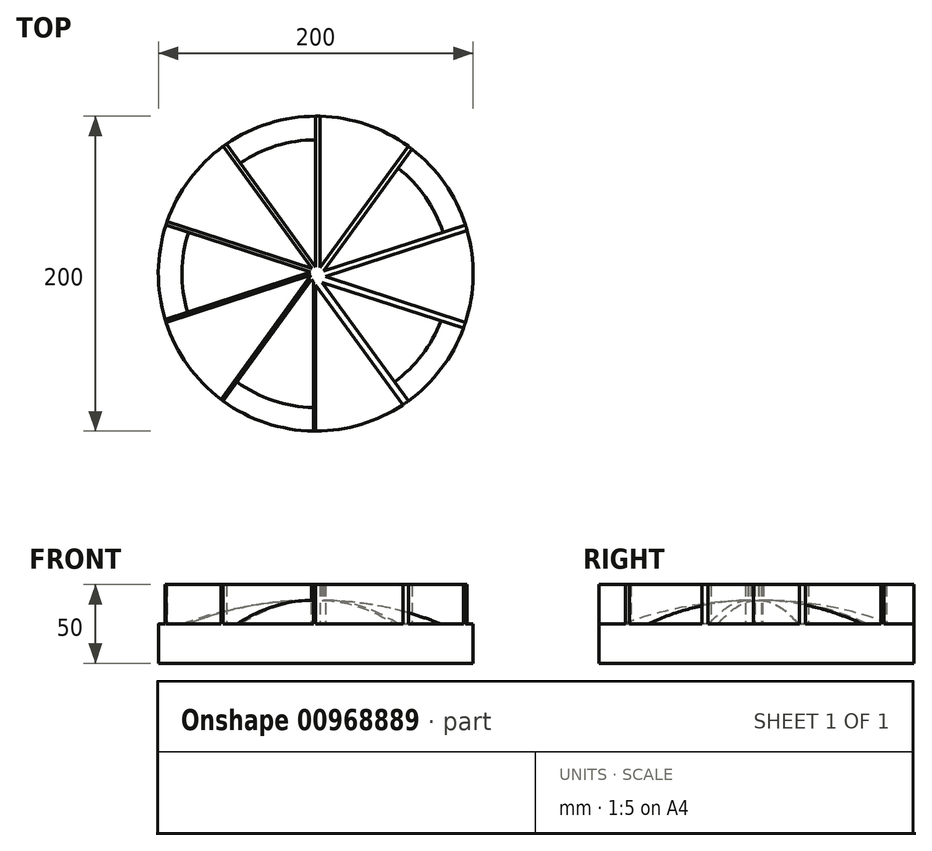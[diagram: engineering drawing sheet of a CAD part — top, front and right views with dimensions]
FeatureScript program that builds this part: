
annotation { "Feature Type Name" : "Feature", "Feature Type Description" : "" }
export const myFeature = defineFeature(function(context is Context, id is Id, definition is map)
    precondition{}
    {
        {
            var Q0;
            Q0=qCreatedBy(makeId("Top.planeOp"),FACE);
            var sketch = newSketch(context, id + "F0", { "sketchPlane" : qUnion([Q0])});
            skCircle(sketch, "E0", {"center": v(0, 0) * mm, "radius": 100 * mm});
            skSolve(sketch);
        }
        {
            var Q0;
            Q0 = qSketchRegion(id + "F0", true);
            extrude(context, id + "F1", {"entities" : qUnion([Q0]), "depth" : 25 * mm, "offsetDistance" : 25 * mm});
        }
        {
            var Q0;
            Q0=makeQuery(id+"F1.opExtrude","CAP_FACE",FACE,{"disambiguationData":[OSD([sQuery(id+"F0.wireOp",EDGE,"E0")])],"isStart":false});
            var sketch = newSketch(context, id + "F2", { "sketchPlane" : qUnion([Q0])});
            skLineSegment(sketch, "E1", {"start": v(0, 0) * mm, "end": v(0, -100) * mm});
            skLineSegment(sketch, "E2.1.0", {"start": v(0, 0) * mm, "end": v(58.78, -80.9) * mm});
            skLineSegment(sketch, "E2.2.0", {"start": v(0, 0) * mm, "end": v(95.1, -30.9) * mm});
            skLineSegment(sketch, "E2.3.0", {"start": v(0, 0) * mm, "end": v(95.1, 30.9) * mm});
            skLineSegment(sketch, "E2.4.0", {"start": v(0, 0) * mm, "end": v(58.78, 80.9) * mm});
            skLineSegment(sketch, "E2.5.0", {"start": v(0, 0) * mm, "end": v(0, 100) * mm});
            skLineSegment(sketch, "E2.6.0", {"start": v(0, 0) * mm, "end": v(-58.78, 80.9) * mm});
            skLineSegment(sketch, "E2.7.0", {"start": v(0, 0) * mm, "end": v(-95.1, 30.9) * mm});
            skLineSegment(sketch, "E2.8.0", {"start": v(0, 0) * mm, "end": v(-95.1, -30.9) * mm});
            skLineSegment(sketch, "E2.9.0", {"start": v(0, 0) * mm, "end": v(-58.78, -80.9) * mm});
            skPoint(sketch, "E2.center", {"position": v(0, 0) * mm});
            skCircle(sketch, "E3", {"center": v(0, 0) * mm, "radius": 2.5 * mm});
            skLineSegment(sketch, "E4.0", {"start": v(-1.5, 0) * mm, "end": v(-1.5, -100) * mm});
            skLineSegment(sketch, "E5.0", {"start": v(-1.42, 1.03) * mm, "end": v(-60.2, -79.87) * mm});
            skLineSegment(sketch, "E6.0", {"start": v(-0.62, 1.9) * mm, "end": v(-95.72, -29) * mm});
            skLineSegment(sketch, "E7.0", {"start": v(0.7, 2.14) * mm, "end": v(-94.41, 33.04) * mm});
            skLineSegment(sketch, "E8.0", {"start": v(2.02, 1.47) * mm, "end": v(-56.76, 82.37) * mm});
            skLineSegment(sketch, "E9.0", {"start": v(2.75, 0) * mm, "end": v(2.75, 100) * mm});
            skLineSegment(sketch, "E10.0", {"start": v(2.43, -1.76) * mm, "end": v(61.2, 79.14) * mm});
            skLineSegment(sketch, "E11.0", {"start": v(1.16, -3.57) * mm, "end": v(96.26, 27.34) * mm});
            skLineSegment(sketch, "E12.0", {"start": v(-1.24, -3.8) * mm, "end": v(93.87, -34.7) * mm});
            skLineSegment(sketch, "E13.0", {"start": v(-3.44, -2.5) * mm, "end": v(55.34, -83.4) * mm});
            skSolve(sketch);
        }
        {
            var Q0;
            {var subQ1=sQuery(id+"F2.wireOp",EDGE,"E1");var subQ5=sQuery(id+"F2.wireOp",EDGE,"E12.0");var subQ6=makeQuery(id+"F2.imprint","INTERSECT",VERTEX,{"derivedFrom":[subQ1,subQ5]});Q0=makeQuery(id+"F2.imprint","IMPRINT",FACE,{"disambiguationData":[TD([[makeQuery(id+"F2.imprint","IMPRINT",EDGE,{"disambiguationData":[TD([[subQ6,-1.0]])],"derivedFrom":subQ1}),1.0]])]});}
            var Q1;
            {var subQ0=sQuery(id+"F2.wireOp",EDGE,"E11.0");var subQ1=sQuery(id+"F2.wireOp",EDGE,"E2.1.0");var subQ2=makeQuery(id+"F2.imprint","INTERSECT",VERTEX,{"derivedFrom":[subQ1,subQ0]});Q1=makeQuery(id+"F2.imprint","IMPRINT",FACE,{"disambiguationData":[TD([[makeQuery(id+"F2.imprint","IMPRINT",EDGE,{"disambiguationData":[TD([[subQ2,-1.0]])],"derivedFrom":subQ1}),1.0]])]});}
            var Q2;
            {var subQ3=sQuery(id+"F2.wireOp",EDGE,"E3");var subQ5=sQuery(id+"F2.wireOp",EDGE,"E2.2.0");var subQ6=makeQuery(id+"F2.imprint","INTERSECT",VERTEX,{"derivedFrom":[subQ5,subQ3]});Q2=makeQuery(id+"F2.imprint","IMPRINT",FACE,{"disambiguationData":[TD([[makeQuery(id+"F2.imprint","IMPRINT",EDGE,{"disambiguationData":[TD([[subQ6,-1.0]])],"derivedFrom":subQ5}),1.0]])]});}
            var Q3;
            {var subQ3=sQuery(id+"F2.wireOp",EDGE,"E3");var subQ5=sQuery(id+"F2.wireOp",EDGE,"E2.3.0");var subQ6=makeQuery(id+"F2.imprint","INTERSECT",VERTEX,{"derivedFrom":[subQ5,subQ3]});Q3=makeQuery(id+"F2.imprint","IMPRINT",FACE,{"disambiguationData":[TD([[makeQuery(id+"F2.imprint","IMPRINT",EDGE,{"disambiguationData":[TD([[subQ6,-1.0]])],"derivedFrom":subQ5}),1.0]])]});}
            var Q4;
            {var subQ0=sQuery(id+"F2.wireOp",EDGE,"E3");var subQ1=sQuery(id+"F2.wireOp",EDGE,"E2.4.0");var subQ2=makeQuery(id+"F2.imprint","INTERSECT",VERTEX,{"derivedFrom":[subQ1,subQ0]});Q4=makeQuery(id+"F2.imprint","IMPRINT",FACE,{"disambiguationData":[TD([[makeQuery(id+"F2.imprint","IMPRINT",EDGE,{"disambiguationData":[TD([[subQ2,-1.0]])],"derivedFrom":subQ1}),1.0]])]});}
            var Q5;
            {var subQ3=sQuery(id+"F2.wireOp",EDGE,"E3");var subQ9=sQuery(id+"F2.wireOp",EDGE,"E2.5.0");var subQ10=makeQuery(id+"F2.imprint","INTERSECT",VERTEX,{"derivedFrom":[subQ9,subQ3]});Q5=makeQuery(id+"F2.imprint","IMPRINT",FACE,{"disambiguationData":[TD([[makeQuery(id+"F2.imprint","IMPRINT",EDGE,{"disambiguationData":[TD([[subQ10,-1.0]])],"derivedFrom":subQ9}),1.0]])]});}
            var Q6;
            {var subQ1=sQuery(id+"F2.wireOp",EDGE,"E2.6.0");var subQ5=sQuery(id+"F2.wireOp",EDGE,"E3");var subQ6=makeQuery(id+"F2.imprint","INTERSECT",VERTEX,{"derivedFrom":[subQ1,subQ5]});Q6=makeQuery(id+"F2.imprint","IMPRINT",FACE,{"disambiguationData":[TD([[makeQuery(id+"F2.imprint","IMPRINT",EDGE,{"disambiguationData":[TD([[subQ6,-1.0]])],"derivedFrom":subQ1}),1.0]])]});}
            var Q7;
            {var subQ0=sQuery(id+"F2.wireOp",EDGE,"E2.8.0");var subQ1=makeQuery(id+"F1.opExtrude","CAP_EDGE",EDGE,{"disambiguationData":[OSD([sQuery(id+"F0.wireOp",EDGE,"E0")])],"isStart":false});var subQ2=makeQuery(id+"F2.imprint","INTERSECT",VERTEX,{"derivedFrom":[subQ1,subQ0]});Q7=makeQuery(id+"F2.imprint","IMPRINT",FACE,{"disambiguationData":[TD([[makeQuery(id+"F2.imprint","IMPRINT",EDGE,{"disambiguationData":[TD([[subQ2,1.0]])],"derivedFrom":subQ0}),-1.0]])]});}
            var Q8;
            {var subQ5=sQuery(id+"F2.wireOp",EDGE,"E2.9.0");var subQ8=makeQuery(id+"F2.imprint","INTERSECT",VERTEX,{"derivedFrom":[subQ5,sQuery(id+"F2.wireOp",EDGE,"E13.0")]});Q8=makeQuery(id+"F2.imprint","IMPRINT",FACE,{"disambiguationData":[TD([[makeQuery(id+"F2.imprint","IMPRINT",EDGE,{"disambiguationData":[TD([[subQ8,1.0]])],"derivedFrom":subQ5}),-1.0]])]});}
            var Q9;
            {var subQ0=sQuery(id+"F2.wireOp",EDGE,"E1");var subQ1=makeQuery(id+"F1.opExtrude","CAP_EDGE",EDGE,{"disambiguationData":[OSD([sQuery(id+"F0.wireOp",EDGE,"E0")])],"isStart":false});var subQ2=makeQuery(id+"F2.imprint","INTERSECT",VERTEX,{"derivedFrom":[subQ1,subQ0]});Q9=makeQuery(id+"F2.imprint","IMPRINT",FACE,{"disambiguationData":[TD([[makeQuery(id+"F2.imprint","IMPRINT",EDGE,{"disambiguationData":[TD([[subQ2,1.0]])],"derivedFrom":subQ0}),-1.0]])]});}
            var Q10;
            {var subQ1=sQuery(id+"F2.wireOp",EDGE,"E2.4.0");var subQ5=sQuery(id+"F2.wireOp",EDGE,"E8.0");var subQ6=makeQuery(id+"F2.imprint","INTERSECT",VERTEX,{"derivedFrom":[subQ1,subQ5]});Q10=makeQuery(id+"F2.imprint","IMPRINT",FACE,{"disambiguationData":[TD([[makeQuery(id+"F2.imprint","IMPRINT",EDGE,{"disambiguationData":[TD([[subQ6,-1.0]])],"derivedFrom":subQ1}),1.0]])]});}
            var Q11;
            {var subQ0=sQuery(id+"F2.wireOp",EDGE,"E9.0");var subQ1=sQuery(id+"F2.wireOp",EDGE,"E2.3.0");var subQ2=makeQuery(id+"F2.imprint","INTERSECT",VERTEX,{"derivedFrom":[subQ1,subQ0]});Q11=makeQuery(id+"F2.imprint","IMPRINT",FACE,{"disambiguationData":[TD([[makeQuery(id+"F2.imprint","IMPRINT",EDGE,{"disambiguationData":[TD([[subQ2,-1.0]])],"derivedFrom":subQ1}),1.0]])]});}
            var Q12;
            {var subQ1=sQuery(id+"F2.wireOp",EDGE,"E2.2.0");var subQ5=sQuery(id+"F2.wireOp",EDGE,"E10.0");var subQ6=makeQuery(id+"F2.imprint","INTERSECT",VERTEX,{"derivedFrom":[subQ1,subQ5]});Q12=makeQuery(id+"F2.imprint","IMPRINT",FACE,{"disambiguationData":[TD([[makeQuery(id+"F2.imprint","IMPRINT",EDGE,{"disambiguationData":[TD([[subQ6,-1.0]])],"derivedFrom":subQ1}),1.0]])]});}
            var Q13;
            {var subQ0=sQuery(id+"F2.wireOp",EDGE,"E3");var subQ1=sQuery(id+"F2.wireOp",EDGE,"E2.4.0");var subQ2=makeQuery(id+"F2.imprint","INTERSECT",VERTEX,{"derivedFrom":[subQ1,subQ0]});Q13=makeQuery(id+"F2.imprint","IMPRINT",FACE,{"disambiguationData":[TD([[makeQuery(id+"F2.imprint","IMPRINT",EDGE,{"disambiguationData":[TD([[subQ2,-1.0]])],"derivedFrom":subQ1}),-1.0]])]});}
            var Q14;
            {var subQ0=sQuery(id+"F2.wireOp",EDGE,"E3");var subQ1=sQuery(id+"F2.wireOp",EDGE,"E2.6.0");var subQ2=makeQuery(id+"F2.imprint","INTERSECT",VERTEX,{"derivedFrom":[subQ1,subQ0]});Q14=makeQuery(id+"F2.imprint","IMPRINT",FACE,{"disambiguationData":[TD([[makeQuery(id+"F2.imprint","IMPRINT",EDGE,{"disambiguationData":[TD([[subQ2,-1.0]])],"derivedFrom":subQ1}),-1.0]])]});}
            var Q15;
            {var subQ0=sQuery(id+"F2.wireOp",EDGE,"E3");var subQ1=sQuery(id+"F2.wireOp",EDGE,"E2.7.0");var subQ2=makeQuery(id+"F2.imprint","INTERSECT",VERTEX,{"derivedFrom":[subQ1,subQ0]});Q15=makeQuery(id+"F2.imprint","IMPRINT",FACE,{"disambiguationData":[TD([[makeQuery(id+"F2.imprint","IMPRINT",EDGE,{"disambiguationData":[TD([[subQ2,-1.0]])],"derivedFrom":subQ1}),-1.0]])]});}
            var Q16;
            {var subQ0=sQuery(id+"F2.wireOp",EDGE,"E3");var subQ1=sQuery(id+"F2.wireOp",EDGE,"E2.8.0");var subQ2=makeQuery(id+"F2.imprint","INTERSECT",VERTEX,{"derivedFrom":[subQ1,subQ0]});Q16=makeQuery(id+"F2.imprint","IMPRINT",FACE,{"disambiguationData":[TD([[makeQuery(id+"F2.imprint","IMPRINT",EDGE,{"disambiguationData":[TD([[subQ2,-1.0]])],"derivedFrom":subQ1}),-1.0]])]});}
            var Q17;
            {var subQ0=sQuery(id+"F2.wireOp",EDGE,"E3");var subQ1=sQuery(id+"F2.wireOp",EDGE,"E2.9.0");var subQ2=makeQuery(id+"F2.imprint","INTERSECT",VERTEX,{"derivedFrom":[subQ1,subQ0]});Q17=makeQuery(id+"F2.imprint","IMPRINT",FACE,{"disambiguationData":[TD([[makeQuery(id+"F2.imprint","IMPRINT",EDGE,{"disambiguationData":[TD([[subQ2,-1.0]])],"derivedFrom":subQ1}),-1.0]])]});}
            var Q18;
            {var subQ0=sQuery(id+"F2.wireOp",EDGE,"E3");var subQ1=sQuery(id+"F2.wireOp",EDGE,"E2.4.0");var subQ2=makeQuery(id+"F2.imprint","INTERSECT",VERTEX,{"derivedFrom":[subQ1,subQ0]});Q18=makeQuery(id+"F2.imprint","IMPRINT",FACE,{"disambiguationData":[TD([[makeQuery(id+"F2.imprint","IMPRINT",EDGE,{"disambiguationData":[TD([[subQ2,-1.0]])],"derivedFrom":subQ1}),1.0]])]});}
            var Q19;
            {var subQ1=sQuery(id+"F2.wireOp",EDGE,"E1");var subQ6=sQuery(id+"F2.wireOp",EDGE,"E12.0");var subQ8=makeQuery(id+"F2.imprint","INTERSECT",VERTEX,{"derivedFrom":[subQ1,subQ6]});Q19=makeQuery(id+"F2.imprint","IMPRINT",FACE,{"disambiguationData":[TD([[makeQuery(id+"F2.imprint","IMPRINT",EDGE,{"disambiguationData":[TD([[subQ8,1.0]])],"derivedFrom":subQ1}),1.0]])]});}
            var Q20;
            {var subQ1=sQuery(id+"F2.wireOp",EDGE,"E2.1.0");var subQ6=sQuery(id+"F2.wireOp",EDGE,"E11.0");var subQ7=makeQuery(id+"F2.imprint","INTERSECT",VERTEX,{"derivedFrom":[subQ1,subQ6]});Q20=makeQuery(id+"F2.imprint","IMPRINT",FACE,{"disambiguationData":[TD([[makeQuery(id+"F2.imprint","IMPRINT",EDGE,{"disambiguationData":[TD([[subQ7,1.0]])],"derivedFrom":subQ1}),1.0]])]});}
            var Q21;
            {var subQ4=sQuery(id+"F2.wireOp",EDGE,"E2.2.0");var subQ6=sQuery(id+"F2.wireOp",EDGE,"E10.0");var subQ8=makeQuery(id+"F2.imprint","INTERSECT",VERTEX,{"derivedFrom":[subQ4,subQ6]});Q21=makeQuery(id+"F2.imprint","IMPRINT",FACE,{"disambiguationData":[TD([[makeQuery(id+"F2.imprint","IMPRINT",EDGE,{"disambiguationData":[TD([[subQ8,1.0]])],"derivedFrom":subQ4}),1.0]])]});}
            var Q22;
            {var subQ3=sQuery(id+"F2.wireOp",EDGE,"E2.3.0");var subQ7=sQuery(id+"F2.wireOp",EDGE,"E9.0");var subQ9=makeQuery(id+"F2.imprint","INTERSECT",VERTEX,{"derivedFrom":[subQ3,subQ7]});Q22=makeQuery(id+"F2.imprint","IMPRINT",FACE,{"disambiguationData":[TD([[makeQuery(id+"F2.imprint","IMPRINT",EDGE,{"disambiguationData":[TD([[subQ9,1.0]])],"derivedFrom":subQ3}),1.0]])]});}
            var Q23;
            {var subQ5=sQuery(id+"F2.wireOp",EDGE,"E1");var subQ6=makeQuery(id+"F2.imprint","INTERSECT",VERTEX,{"derivedFrom":[subQ5,sQuery(id+"F2.wireOp",EDGE,"E12.0")]});Q23=makeQuery(id+"F2.imprint","IMPRINT",FACE,{"disambiguationData":[TD([[makeQuery(id+"F2.imprint","IMPRINT",EDGE,{"disambiguationData":[TD([[subQ6,1.0]])],"derivedFrom":subQ5}),-1.0]])]});}
            var Q24;
            {var subQ0=sQuery(id+"F2.wireOp",EDGE,"E13.0");var subQ1=sQuery(id+"F2.wireOp",EDGE,"E2.9.0");var subQ2=makeQuery(id+"F2.imprint","INTERSECT",VERTEX,{"derivedFrom":[subQ1,subQ0]});Q24=makeQuery(id+"F2.imprint","IMPRINT",FACE,{"disambiguationData":[TD([[makeQuery(id+"F2.imprint","IMPRINT",EDGE,{"disambiguationData":[TD([[subQ2,1.0]])],"derivedFrom":subQ1}),1.0]])]});}
            var Q25;
            {var subQ1=sQuery(id+"F2.wireOp",EDGE,"E1");var subQ3=sQuery(id+"F2.wireOp",EDGE,"E3");var subQ4=makeQuery(id+"F2.imprint","INTERSECT",VERTEX,{"derivedFrom":[subQ1,subQ3]});Q25=makeQuery(id+"F2.imprint","IMPRINT",FACE,{"disambiguationData":[TD([[makeQuery(id+"F2.imprint","IMPRINT",EDGE,{"disambiguationData":[TD([[subQ4,-1.0]])],"derivedFrom":subQ3}),1.0]])]});}
            var Q26;
            {var subQ1=sQuery(id+"F2.wireOp",EDGE,"E2.1.0");var subQ3=sQuery(id+"F2.wireOp",EDGE,"E3");var subQ4=makeQuery(id+"F2.imprint","INTERSECT",VERTEX,{"derivedFrom":[subQ1,subQ3]});Q26=makeQuery(id+"F2.imprint","IMPRINT",FACE,{"disambiguationData":[TD([[makeQuery(id+"F2.imprint","IMPRINT",EDGE,{"disambiguationData":[TD([[subQ4,-1.0]])],"derivedFrom":subQ3}),1.0]])]});}
            var Q27;
            {var subQ1=sQuery(id+"F2.wireOp",EDGE,"E2.2.0");var subQ3=sQuery(id+"F2.wireOp",EDGE,"E3");var subQ4=makeQuery(id+"F2.imprint","INTERSECT",VERTEX,{"derivedFrom":[subQ1,subQ3]});Q27=makeQuery(id+"F2.imprint","IMPRINT",FACE,{"disambiguationData":[TD([[makeQuery(id+"F2.imprint","IMPRINT",EDGE,{"disambiguationData":[TD([[subQ4,-1.0]])],"derivedFrom":subQ3}),1.0]])]});}
            var Q28;
            {var subQ3=sQuery(id+"F2.wireOp",EDGE,"E3");var subQ6=makeQuery(id+"F2.imprint","INTERSECT",VERTEX,{"derivedFrom":[subQ3,sQuery(id+"F2.wireOp",EDGE,"E8.0")]});Q28=makeQuery(id+"F2.imprint","IMPRINT",FACE,{"disambiguationData":[TD([[makeQuery(id+"F2.imprint","IMPRINT",EDGE,{"disambiguationData":[TD([[subQ6,1.0]])],"derivedFrom":subQ3}),1.0]])]});}
            var Q29;
            {var subQ0=sQuery(id+"F2.wireOp",EDGE,"E2.5.0");var subQ5=makeQuery(id+"F2.imprint","INTERSECT",VERTEX,{"derivedFrom":[subQ0,sQuery(id+"F2.wireOp",EDGE,"E7.0")]});Q29=makeQuery(id+"F2.imprint","IMPRINT",FACE,{"disambiguationData":[TD([[makeQuery(id+"F2.imprint","IMPRINT",EDGE,{"disambiguationData":[TD([[subQ5,-1.0]])],"derivedFrom":subQ0}),-1.0]])]});}
            var Q30;
            {var subQ1=sQuery(id+"F2.wireOp",EDGE,"E2.6.0");var subQ7=makeQuery(id+"F2.imprint","INTERSECT",VERTEX,{"derivedFrom":[subQ1,sQuery(id+"F2.wireOp",EDGE,"E6.0")]});Q30=makeQuery(id+"F2.imprint","IMPRINT",FACE,{"disambiguationData":[TD([[makeQuery(id+"F2.imprint","IMPRINT",EDGE,{"disambiguationData":[TD([[subQ7,-1.0]])],"derivedFrom":subQ1}),-1.0]])]});}
            var Q31;
            {var subQ1=sQuery(id+"F2.wireOp",EDGE,"E2.7.0");var subQ8=makeQuery(id+"F2.imprint","INTERSECT",VERTEX,{"derivedFrom":[subQ1,sQuery(id+"F2.wireOp",EDGE,"E5.0")]});Q31=makeQuery(id+"F2.imprint","IMPRINT",FACE,{"disambiguationData":[TD([[makeQuery(id+"F2.imprint","IMPRINT",EDGE,{"disambiguationData":[TD([[subQ8,-1.0]])],"derivedFrom":subQ1}),-1.0]])]});}
            var Q32;
            {var subQ0=sQuery(id+"F2.wireOp",EDGE,"E2.8.0");var subQ3=makeQuery(id+"F2.imprint","INTERSECT",VERTEX,{"derivedFrom":[subQ0,sQuery(id+"F2.wireOp",EDGE,"E4.0")]});Q32=makeQuery(id+"F2.imprint","IMPRINT",FACE,{"disambiguationData":[TD([[makeQuery(id+"F2.imprint","IMPRINT",EDGE,{"disambiguationData":[TD([[subQ3,-1.0]])],"derivedFrom":subQ0}),-1.0]])]});}
            var Q33;
            {var subQ0=sQuery(id+"F2.wireOp",EDGE,"E2.9.0");var subQ5=sQuery(id+"F2.wireOp",EDGE,"E3");var subQ6=makeQuery(id+"F2.imprint","INTERSECT",VERTEX,{"derivedFrom":[subQ0,subQ5]});Q33=makeQuery(id+"F2.imprint","IMPRINT",FACE,{"disambiguationData":[TD([[makeQuery(id+"F2.imprint","IMPRINT",EDGE,{"disambiguationData":[TD([[subQ6,1.0]])],"derivedFrom":subQ5}),1.0]])]});}
            var Q34;
            {var subQ1=sQuery(id+"F2.wireOp",EDGE,"E1");var subQ3=sQuery(id+"F2.wireOp",EDGE,"E3");var subQ4=makeQuery(id+"F2.imprint","INTERSECT",VERTEX,{"derivedFrom":[subQ1,subQ3]});Q34=makeQuery(id+"F2.imprint","IMPRINT",FACE,{"disambiguationData":[TD([[makeQuery(id+"F2.imprint","IMPRINT",EDGE,{"disambiguationData":[TD([[subQ4,1.0]])],"derivedFrom":subQ3}),1.0]])]});}
            var Q35;
            {var subQ0=sQuery(id+"F2.wireOp",EDGE,"E4.0");var subQ1=sQuery(id+"F2.wireOp",EDGE,"E2.8.0");var subQ2=makeQuery(id+"F2.imprint","INTERSECT",VERTEX,{"derivedFrom":[subQ1,subQ0]});Q35=makeQuery(id+"F2.imprint","IMPRINT",FACE,{"disambiguationData":[TD([[makeQuery(id+"F2.imprint","IMPRINT",EDGE,{"disambiguationData":[TD([[subQ2,-1.0]])],"derivedFrom":subQ1}),1.0]])]});}
            var Q36;
            {var subQ0=sQuery(id+"F2.wireOp",EDGE,"E5.0");var subQ1=sQuery(id+"F2.wireOp",EDGE,"E2.7.0");var subQ2=makeQuery(id+"F2.imprint","INTERSECT",VERTEX,{"derivedFrom":[subQ1,subQ0]});Q36=makeQuery(id+"F2.imprint","IMPRINT",FACE,{"disambiguationData":[TD([[makeQuery(id+"F2.imprint","IMPRINT",EDGE,{"disambiguationData":[TD([[subQ2,-1.0]])],"derivedFrom":subQ1}),1.0]])]});}
            var Q37;
            {var subQ0=sQuery(id+"F2.wireOp",EDGE,"E6.0");var subQ1=sQuery(id+"F2.wireOp",EDGE,"E2.6.0");var subQ2=makeQuery(id+"F2.imprint","INTERSECT",VERTEX,{"derivedFrom":[subQ1,subQ0]});Q37=makeQuery(id+"F2.imprint","IMPRINT",FACE,{"disambiguationData":[TD([[makeQuery(id+"F2.imprint","IMPRINT",EDGE,{"disambiguationData":[TD([[subQ2,-1.0]])],"derivedFrom":subQ1}),1.0]])]});}
            var Q38;
            {var subQ0=sQuery(id+"F2.wireOp",EDGE,"E7.0");var subQ1=sQuery(id+"F2.wireOp",EDGE,"E2.5.0");var subQ2=makeQuery(id+"F2.imprint","INTERSECT",VERTEX,{"derivedFrom":[subQ1,subQ0]});Q38=makeQuery(id+"F2.imprint","IMPRINT",FACE,{"disambiguationData":[TD([[makeQuery(id+"F2.imprint","IMPRINT",EDGE,{"disambiguationData":[TD([[subQ2,-1.0]])],"derivedFrom":subQ1}),1.0]])]});}
            extrude(context, id + "F3", {"entities" : qUnion([Q0, Q1, Q2, Q3, Q4, Q5, Q6, Q7, Q8, Q9, Q10, Q11, Q12, Q13, Q14, Q15, Q16, Q17, Q18, Q19, Q20, Q21, Q22, Q23, Q24, Q25, Q26, Q27, Q28, Q29, Q30, Q31, Q32, Q33, Q34, Q35, Q36, Q37, Q38]), "operationType" : NewBodyOperationType.ADD, "depth" : 25 * mm, "offsetDistance" : 25 * mm});
        }
        {
            var Q0;
            Q0=qCreatedBy(makeId("Right.planeOp"),FACE);
            var sketch = newSketch(context, id + "F4", { "sketchPlane" : qUnion([Q0])});
            skLineSegment(sketch, "E14", {"start": v(0, 0) * mm, "end": v(0, 67.34) * mm});
            skLineSegment(sketch, "E15", {"start": v(0, 0) * mm, "end": v(0, 40) * mm});
            skLineSegment(sketch, "E16", {"start": v(0, 0) * mm, "end": v(0, 20) * mm});
            skLineSegment(sketch, "E17", {"start": v(0, 25) * mm, "end": v(0, 0) * mm});
            skLineSegment(sketch, "E18", {"start": v(0, 25) * mm, "end": v(-85, 25) * mm});
            skArc(sketch, "E19", {"start": v(0, 40) * mm, "mid": v(-43.21, 36.53) * mm, "end": v(-85, 25) * mm});
            skSolve(sketch);
        }
        {
            var Q0;
            Q0 = qSketchRegion(id + "F4", true);
            var Q1;
            Q1=sQuery(id+"F4.wireOp",EDGE,"E14");
            revolve(context, id + "F5", {"operationType" : NewBodyOperationType.ADD, "surfaceOperationType" : NewSurfaceOperationType.NEW, "entities" : qUnion([Q0]), "axis" : qUnion([Q1]), "revolveType" : RevolveType.FULL});
        }
        {
            var Q0;
            {var subQ0=sQuery(id+"F2.wireOp",EDGE,"E1");var subQ1=makeQuery(id+"F1.opExtrude","CAP_EDGE",EDGE,{"disambiguationData":[OSD([sQuery(id+"F0.wireOp",EDGE,"E0")])],"isStart":false});var subQ2=makeQuery(id+"F2.imprint","INTERSECT",VERTEX,{"derivedFrom":[subQ1,subQ0]});Q0=makeQuery(id+"F2.imprint","IMPRINT",FACE,{"disambiguationData":[TD([[makeQuery(id+"F2.imprint","IMPRINT",EDGE,{"disambiguationData":[TD([[subQ2,1.0]])],"derivedFrom":subQ0}),1.0]])]});}
            var Q1;
            {var subQ0=sQuery(id+"F2.wireOp",EDGE,"E2.2.0");var subQ1=makeQuery(id+"F1.opExtrude","CAP_EDGE",EDGE,{"disambiguationData":[OSD([sQuery(id+"F0.wireOp",EDGE,"E0")])],"isStart":false});var subQ2=makeQuery(id+"F2.imprint","INTERSECT",VERTEX,{"derivedFrom":[subQ1,subQ0]});Q1=makeQuery(id+"F2.imprint","IMPRINT",FACE,{"disambiguationData":[TD([[makeQuery(id+"F2.imprint","IMPRINT",EDGE,{"disambiguationData":[TD([[subQ2,1.0]])],"derivedFrom":subQ0}),1.0]])]});}
            var Q2;
            {var subQ0=sQuery(id+"F2.wireOp",EDGE,"E2.4.0");var subQ1=makeQuery(id+"F1.opExtrude","CAP_EDGE",EDGE,{"disambiguationData":[OSD([sQuery(id+"F0.wireOp",EDGE,"E0")])],"isStart":false});var subQ2=makeQuery(id+"F2.imprint","INTERSECT",VERTEX,{"derivedFrom":[subQ1,subQ0]});Q2=makeQuery(id+"F2.imprint","IMPRINT",FACE,{"disambiguationData":[TD([[makeQuery(id+"F2.imprint","IMPRINT",EDGE,{"disambiguationData":[TD([[subQ2,1.0]])],"derivedFrom":subQ0}),1.0]])]});}
            var Q3;
            {var subQ0=sQuery(id+"F2.wireOp",EDGE,"E2.6.0");var subQ1=makeQuery(id+"F1.opExtrude","CAP_EDGE",EDGE,{"disambiguationData":[OSD([sQuery(id+"F0.wireOp",EDGE,"E0")])],"isStart":false});var subQ2=makeQuery(id+"F2.imprint","INTERSECT",VERTEX,{"derivedFrom":[subQ1,subQ0]});Q3=makeQuery(id+"F2.imprint","IMPRINT",FACE,{"disambiguationData":[TD([[makeQuery(id+"F2.imprint","IMPRINT",EDGE,{"disambiguationData":[TD([[subQ2,1.0]])],"derivedFrom":subQ0}),1.0]])]});}
            var Q4;
            {var subQ0=sQuery(id+"F2.wireOp",EDGE,"E2.8.0");var subQ1=makeQuery(id+"F1.opExtrude","CAP_EDGE",EDGE,{"disambiguationData":[OSD([sQuery(id+"F0.wireOp",EDGE,"E0")])],"isStart":false});var subQ2=makeQuery(id+"F2.imprint","INTERSECT",VERTEX,{"derivedFrom":[subQ1,subQ0]});Q4=makeQuery(id+"F2.imprint","IMPRINT",FACE,{"disambiguationData":[TD([[makeQuery(id+"F2.imprint","IMPRINT",EDGE,{"disambiguationData":[TD([[subQ2,1.0]])],"derivedFrom":subQ0}),1.0]])]});}
            extrude(context, id + "F6", {"entities" : qUnion([Q0, Q1, Q2, Q3, Q4]), "operationType" : NewBodyOperationType.REMOVE, "depth" : 25 * mm, "offsetDistance" : 25 * mm});
        }
    });
